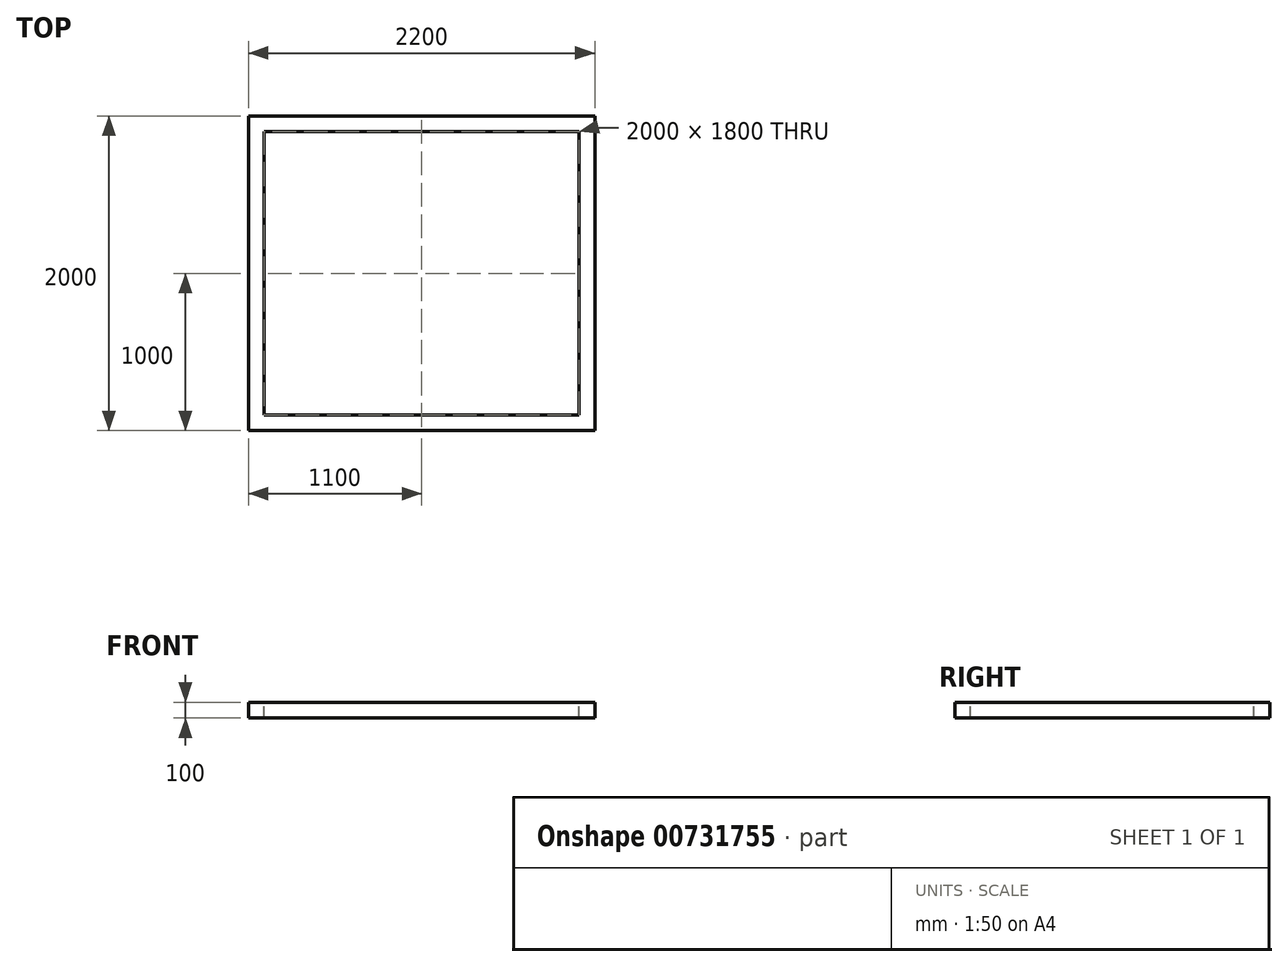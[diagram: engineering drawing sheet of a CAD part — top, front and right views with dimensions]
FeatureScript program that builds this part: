
annotation { "Feature Type Name" : "Feature", "Feature Type Description" : "" }
export const myFeature = defineFeature(function(context is Context, id is Id, definition is map)
    precondition{}
    {
        {
            var Q0;
            Q0=qCreatedBy(makeId("Top.planeOp"),FACE);
            var sketch = newSketch(context, id + "F0", { "sketchPlane" : qUnion([Q0])});
            skLineSegment(sketch, "E0.bottom", {"start": v(1200, -1100) * mm, "end": v(-1200, -1100) * mm});
            skLineSegment(sketch, "E0.top", {"start": v(1200, 1100) * mm, "end": v(-1200, 1100) * mm});
            skLineSegment(sketch, "E0.left", {"start": v(1200, -1100) * mm, "end": v(1200, 1100) * mm});
            skLineSegment(sketch, "E0.right", {"start": v(-1200, -1100) * mm, "end": v(-1200, 1100) * mm});
            skPoint(sketch, "E0.middle", {"position": v(0, 0) * mm});
            skSolve(sketch);
        }
        {
            var Q0;
            Q0=makeQuery(id+"F0.imprint","IMPRINT",FACE,{"disambiguationData":[TD([[makeQuery(id+"F0.imprint","IMPRINT",EDGE,{"derivedFrom":sQuery(id+"F0.wireOp",EDGE,"E0.bottom")}),-1.0]])]});
            extrude(context, id + "F1", {"entities" : qUnion([Q0]), "depth" : 100 * mm, "offsetDistance" : 25 * mm});
        }
        {
            var Q0;
            Q0=makeQuery(id+"F1.opExtrude","CAP_FACE",FACE,{"disambiguationData":[OSD([sQuery(id+"F0.wireOp",EDGE,"E0.bottom"),sQuery(id+"F0.wireOp",EDGE,"E0.top"),sQuery(id+"F0.wireOp",EDGE,"E0.left"),sQuery(id+"F0.wireOp",EDGE,"E0.right")])],"isStart":false});
            var sketch = newSketch(context, id + "F2", { "sketchPlane" : qUnion([Q0])});
            skLineSegment(sketch, "E1.0", {"start": v(1100, -1000) * mm, "end": v(1100, 1000) * mm});
            skLineSegment(sketch, "E1.1", {"start": v(1100, 1000) * mm, "end": v(-1100, 1000) * mm});
            skLineSegment(sketch, "E1.2", {"start": v(-1100, -1000) * mm, "end": v(-1100, 1000) * mm});
            skLineSegment(sketch, "E2.0", {"start": v(1100, -1000) * mm, "end": v(-1100, -1000) * mm});
            skLineSegment(sketch, "E3.0", {"start": v(1000, 900) * mm, "end": v(-1000, 900) * mm});
            skLineSegment(sketch, "E3.1", {"start": v(1000, -900) * mm, "end": v(1000, 900) * mm});
            skLineSegment(sketch, "E3.2", {"start": v(1000, -900) * mm, "end": v(-1000, -900) * mm});
            skLineSegment(sketch, "E3.3", {"start": v(-1000, -900) * mm, "end": v(-1000, 900) * mm});
            skSolve(sketch);
        }
        {
            var Q0;
            Q0=makeQuery(id+"F2.imprint","IMPRINT",FACE,{"disambiguationData":[TD([[makeQuery(id+"F2.imprint","IMPRINT",EDGE,{"derivedFrom":sQuery(id+"F2.wireOp",EDGE,"E1.0")}),-1.0]])]});
            extrude(context, id + "F3", {"entities" : qUnion([Q0]), "operationType" : NewBodyOperationType.REMOVE, "endBound" : BoundingType.THROUGH_ALL, "oppositeDirection" : true, "depth" : 25 * mm, "offsetDistance" : 25 * mm});
        }
        {
            var Q0;
            Q0=makeQuery(id+"F2.imprint","IMPRINT",FACE,{"disambiguationData":[TD([[makeQuery(id+"F2.imprint","IMPRINT",EDGE,{"derivedFrom":sQuery(id+"F2.wireOp",EDGE,"E3.0")}),1.0]])]});
            extrude(context, id + "F4", {"entities" : qUnion([Q0]), "operationType" : NewBodyOperationType.REMOVE, "endBound" : BoundingType.THROUGH_ALL, "oppositeDirection" : true, "depth" : 25 * mm, "offsetDistance" : 25 * mm});
        }
    });
